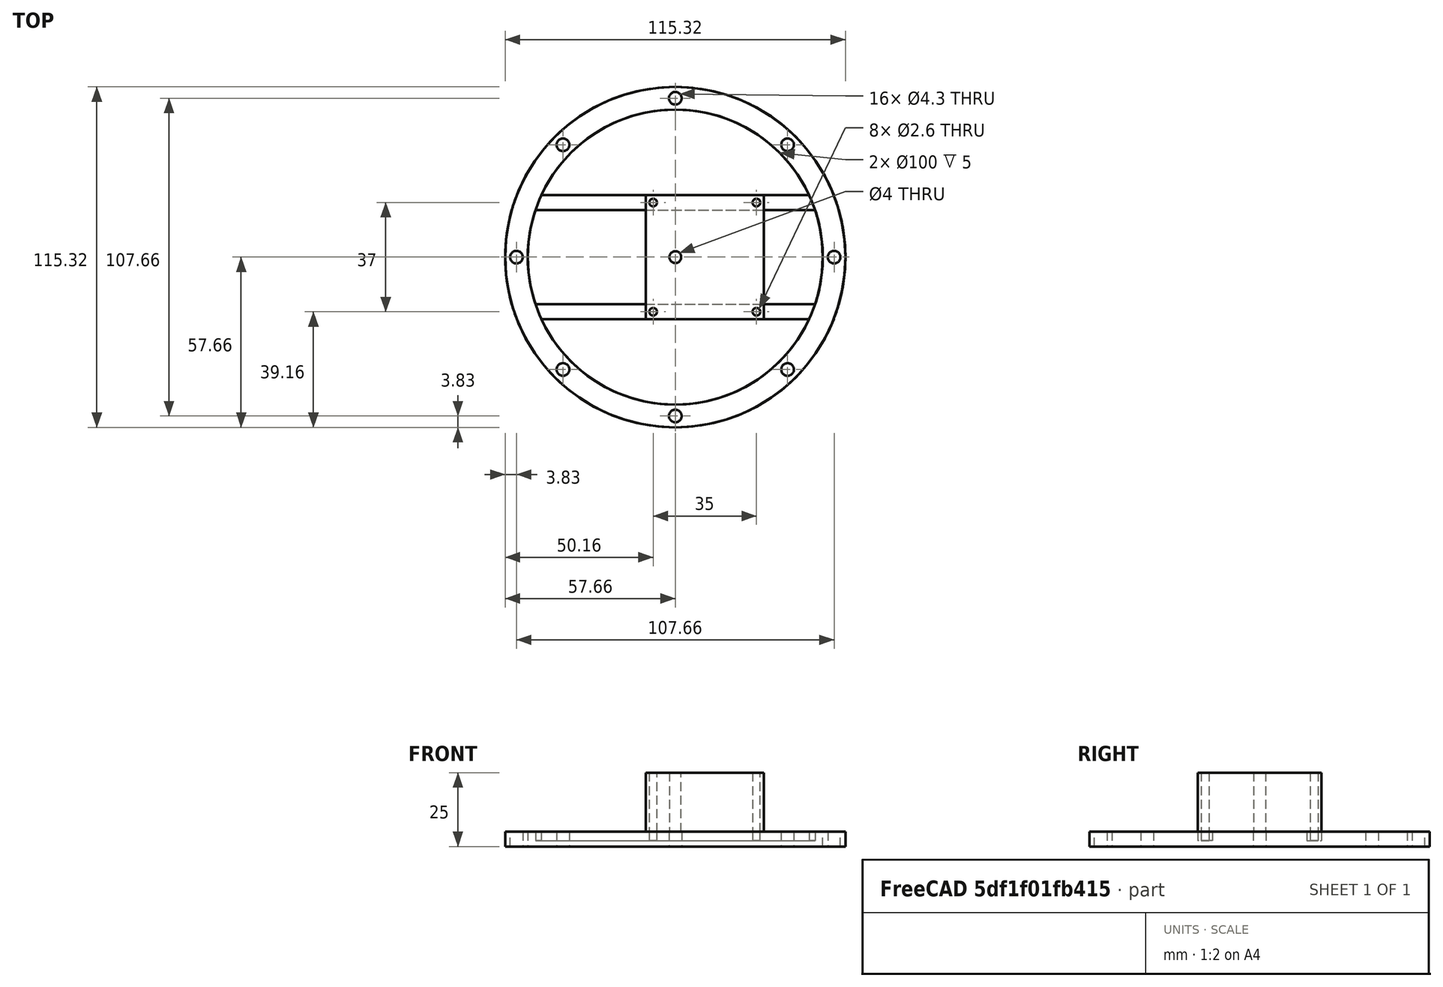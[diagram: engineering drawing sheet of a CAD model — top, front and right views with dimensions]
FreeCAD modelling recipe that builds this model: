
FCSTD DOCUMENT  (FreeCAD 0.20R)
Label: XL30ColumnAttachmentRing_PCBKicker01
License: All rights reserved
LicenseURL: http://en.wikipedia.org/wiki/All_rights_reserved
objects: Part::Cylinder×30, TechDraw::DrawViewDimension×23, Part::Compound×20, Part::Cut×7, TechDraw::DrawProjGroupItem×4, Part::Box×3, Part::MultiFuse×2, TechDraw::DrawSVGTemplate×2, TechDraw::DrawProjGroup×2, TechDraw::DrawPage×2, Part::MultiCommon×1, TechDraw::DrawViewSection×1, TechDraw::DrawViewAnnotation×1
note: 63 computed .brp shape members not serialized (recipe doc carries the construction recipe); baked Part::Feature solids carry a one-line shape summary decoded from their .brp
EXTERNAL_REF file=XL30ColumnAttachmentRing01.FCStd obj=Spreadsheet

FEATURE [Part::Cylinder] Cylinder
  Angle = 360
  AttacherType = Attacher::AttachEngine3D
  FirstAngle = 0
  Height = 5
  Radius = 57.66
  SecondAngle = 0
  expr: Height = <<XL30ColumnAttachmentRing01>>#<<AttachmentRing01>>.ring_thickness
  expr: Radius = <<XL30ColumnAttachmentRing01>>#<<AttachmentRing01>>.ring_od / 2
FEATURE [Part::Cylinder] Cylinder001
  Angle = 360
  AttacherType = Attacher::AttachEngine3D
  FirstAngle = 0
  Height = 5
  Radius = 50
  SecondAngle = 0
  expr: Height = <<XL30ColumnAttachmentRing01>>#<<AttachmentRing01>>.ring_thickness
  expr: Radius = <<XL30ColumnAttachmentRing01>>#<<AttachmentRing01>>.ring_id / 2
FEATURE [Part::Cut] Cut
  Base = -> Cylinder
  Tool = -> Cylinder001
FEATURE [Part::Cylinder] Cylinder002
  Angle = 360
  AttacherType = Attacher::AttachEngine3D
  FirstAngle = 0
  Height = 5
  Placement = pos=(53.83,0,0) rot=(0,0,1;0rad)
  Radius = 2.15
  SecondAngle = 0
  expr: .Placement.Base.x = (<<XL30ColumnAttachmentRing01>>#<<AttachmentRing01>>.ring_od + <<XL30ColumnAttachmentRing01>>#<<AttachmentRing01>>.ring_id) / 4
  expr: Height = <<XL30ColumnAttachmentRing01>>#<<AttachmentRing01>>.ring_thickness
FEATURE [Part::Compound] Compound
  Links = -> [Cylinder002]
FEATURE [Part::Cylinder] Cylinder003
  Angle = 360
  AttacherType = Attacher::AttachEngine3D
  FirstAngle = 0
  Height = 5
  Placement = pos=(53.83,0,0) rot=(0,0,1;0rad)
  Radius = 2.15
  SecondAngle = 0
  expr: .Placement.Base.x = (<<XL30ColumnAttachmentRing01>>#<<AttachmentRing01>>.ring_od + <<XL30ColumnAttachmentRing01>>#<<AttachmentRing01>>.ring_id) / 4
  expr: Height = <<XL30ColumnAttachmentRing01>>#<<AttachmentRing01>>.ring_thickness
FEATURE [Part::Compound] Compound001
  Links = -> [Cylinder003]
  Placement = pos=(0,0,0) rot=(0,0,1;0.785398rad)
FEATURE [Part::Cylinder] Cylinder004
  Angle = 360
  AttacherType = Attacher::AttachEngine3D
  FirstAngle = 0
  Height = 5
  Placement = pos=(53.83,0,0) rot=(0,0,1;0rad)
  Radius = 2.15
  SecondAngle = 0
  expr: .Placement.Base.x = (<<XL30ColumnAttachmentRing01>>#<<AttachmentRing01>>.ring_od + <<XL30ColumnAttachmentRing01>>#<<AttachmentRing01>>.ring_id) / 4
  expr: Height = <<XL30ColumnAttachmentRing01>>#<<AttachmentRing01>>.ring_thickness
FEATURE [Part::Compound] Compound002
  Links = -> [Cylinder004]
  Placement = pos=(0,0,0) rot=(0,0,1;1.5708rad)
FEATURE [Part::Cylinder] Cylinder005
  Angle = 360
  AttacherType = Attacher::AttachEngine3D
  FirstAngle = 0
  Height = 5
  Placement = pos=(53.83,0,0) rot=(0,0,1;0rad)
  Radius = 2.15
  SecondAngle = 0
  expr: .Placement.Base.x = (<<XL30ColumnAttachmentRing01>>#<<AttachmentRing01>>.ring_od + <<XL30ColumnAttachmentRing01>>#<<AttachmentRing01>>.ring_id) / 4
  expr: Height = <<XL30ColumnAttachmentRing01>>#<<AttachmentRing01>>.ring_thickness
FEATURE [Part::Compound] Compound003
  Links = -> [Cylinder005]
  Placement = pos=(0,0,0) rot=(0,0,1;2.35619rad)
FEATURE [Part::Cylinder] Cylinder006
  Angle = 360
  AttacherType = Attacher::AttachEngine3D
  FirstAngle = 0
  Height = 5
  Placement = pos=(53.83,0,0) rot=(0,0,1;0rad)
  Radius = 2.15
  SecondAngle = 0
  expr: .Placement.Base.x = (<<XL30ColumnAttachmentRing01>>#<<AttachmentRing01>>.ring_od + <<XL30ColumnAttachmentRing01>>#<<AttachmentRing01>>.ring_id) / 4
  expr: Height = <<XL30ColumnAttachmentRing01>>#<<AttachmentRing01>>.ring_thickness
FEATURE [Part::Compound] Compound004
  Links = -> [Cylinder006]
  Placement = pos=(0,0,0) rot=(0,0,1;3.14159rad)
FEATURE [Part::Cylinder] Cylinder007
  Angle = 360
  AttacherType = Attacher::AttachEngine3D
  FirstAngle = 0
  Height = 5
  Placement = pos=(53.83,0,0) rot=(0,0,1;0rad)
  Radius = 2.15
  SecondAngle = 0
  expr: .Placement.Base.x = (<<XL30ColumnAttachmentRing01>>#<<AttachmentRing01>>.ring_od + <<XL30ColumnAttachmentRing01>>#<<AttachmentRing01>>.ring_id) / 4
  expr: Height = <<XL30ColumnAttachmentRing01>>#<<AttachmentRing01>>.ring_thickness
FEATURE [Part::Compound] Compound005
  Links = -> [Cylinder007]
  Placement = pos=(0,0,0) rot=(0,0,1;3.92699rad)
FEATURE [Part::Cylinder] Cylinder008
  Angle = 360
  AttacherType = Attacher::AttachEngine3D
  FirstAngle = 0
  Height = 5
  Placement = pos=(53.83,0,0) rot=(0,0,1;0rad)
  Radius = 2.15
  SecondAngle = 0
  expr: .Placement.Base.x = (<<XL30ColumnAttachmentRing01>>#<<AttachmentRing01>>.ring_od + <<XL30ColumnAttachmentRing01>>#<<AttachmentRing01>>.ring_id) / 4
  expr: Height = <<XL30ColumnAttachmentRing01>>#<<AttachmentRing01>>.ring_thickness
FEATURE [Part::Compound] Compound006
  Links = -> [Cylinder008]
  Placement = pos=(0,0,0) rot=(0,0,1;4.71239rad)
FEATURE [Part::Cylinder] Cylinder009
  Angle = 360
  AttacherType = Attacher::AttachEngine3D
  FirstAngle = 0
  Height = 5
  Placement = pos=(53.83,0,0) rot=(0,0,1;0rad)
  Radius = 2.15
  SecondAngle = 0
  expr: .Placement.Base.x = (<<XL30ColumnAttachmentRing01>>#<<AttachmentRing01>>.ring_od + <<XL30ColumnAttachmentRing01>>#<<AttachmentRing01>>.ring_id) / 4
  expr: Height = <<XL30ColumnAttachmentRing01>>#<<AttachmentRing01>>.ring_thickness
FEATURE [Part::Compound] Compound007
  Links = -> [Cylinder009]
  Placement = pos=(0,0,0) rot=(0,0,1;5.49779rad)
FEATURE [Part::Compound] Compound008  label="M4ThroughHoles"
  Links = -> [Compound,Compound001,Compound002,Compound003,Compound004,Compound005,Compound006,Compound007]
FEATURE [Part::Cut] Cut001  label="OuterBaseRing"
  Base = -> Cut
  Tool = -> Compound008
FEATURE [Part::Cylinder] Cylinder010
  Angle = 360
  AttacherType = Attacher::AttachEngine3D
  FirstAngle = 0
  Height = 5
  Radius = 57.66
  SecondAngle = 0
  expr: Height = <<XL30ColumnAttachmentRing01>>#<<AttachmentRing01>>.ring_thickness
  expr: Radius = <<XL30ColumnAttachmentRing01>>#<<AttachmentRing01>>.ring_od / 2
FEATURE [Part::Cylinder] Cylinder011
  Angle = 360
  AttacherType = Attacher::AttachEngine3D
  FirstAngle = 0
  Height = 5
  Radius = 50
  SecondAngle = 0
  expr: Height = <<XL30ColumnAttachmentRing01>>#<<AttachmentRing01>>.ring_thickness
  expr: Radius = <<XL30ColumnAttachmentRing01>>#<<AttachmentRing01>>.ring_id / 2
FEATURE [Part::Cut] Cut002
  Base = -> Cylinder010
  Tool = -> Cylinder011
FEATURE [Part::Cylinder] Cylinder012
  Angle = 360
  AttacherType = Attacher::AttachEngine3D
  FirstAngle = 0
  Height = 5
  Placement = pos=(53.83,0,0) rot=(0,0,1;0rad)
  Radius = 2.15
  SecondAngle = 0
  expr: .Placement.Base.x = (<<XL30ColumnAttachmentRing01>>#<<AttachmentRing01>>.ring_od + <<XL30ColumnAttachmentRing01>>#<<AttachmentRing01>>.ring_id) / 4
  expr: Height = <<XL30ColumnAttachmentRing01>>#<<AttachmentRing01>>.ring_thickness
FEATURE [Part::Compound] Compound009
  Links = -> [Cylinder012]
FEATURE [Part::Cylinder] Cylinder013
  Angle = 360
  AttacherType = Attacher::AttachEngine3D
  FirstAngle = 0
  Height = 5
  Placement = pos=(53.83,0,0) rot=(0,0,1;0rad)
  Radius = 2.15
  SecondAngle = 0
  expr: .Placement.Base.x = (<<XL30ColumnAttachmentRing01>>#<<AttachmentRing01>>.ring_od + <<XL30ColumnAttachmentRing01>>#<<AttachmentRing01>>.ring_id) / 4
  expr: Height = <<XL30ColumnAttachmentRing01>>#<<AttachmentRing01>>.ring_thickness
FEATURE [Part::Compound] Compound010
  Links = -> [Cylinder013]
  Placement = pos=(0,0,0) rot=(0,0,1;0.785398rad)
FEATURE [Part::Cylinder] Cylinder014
  Angle = 360
  AttacherType = Attacher::AttachEngine3D
  FirstAngle = 0
  Height = 5
  Placement = pos=(53.83,0,0) rot=(0,0,1;0rad)
  Radius = 2.15
  SecondAngle = 0
  expr: .Placement.Base.x = (<<XL30ColumnAttachmentRing01>>#<<AttachmentRing01>>.ring_od + <<XL30ColumnAttachmentRing01>>#<<AttachmentRing01>>.ring_id) / 4
  expr: Height = <<XL30ColumnAttachmentRing01>>#<<AttachmentRing01>>.ring_thickness
FEATURE [Part::Compound] Compound011
  Links = -> [Cylinder014]
  Placement = pos=(0,0,0) rot=(0,0,1;1.5708rad)
FEATURE [Part::Cylinder] Cylinder015
  Angle = 360
  AttacherType = Attacher::AttachEngine3D
  FirstAngle = 0
  Height = 5
  Placement = pos=(53.83,0,0) rot=(0,0,1;0rad)
  Radius = 2.15
  SecondAngle = 0
  expr: .Placement.Base.x = (<<XL30ColumnAttachmentRing01>>#<<AttachmentRing01>>.ring_od + <<XL30ColumnAttachmentRing01>>#<<AttachmentRing01>>.ring_id) / 4
  expr: Height = <<XL30ColumnAttachmentRing01>>#<<AttachmentRing01>>.ring_thickness
FEATURE [Part::Compound] Compound012
  Links = -> [Cylinder015]
  Placement = pos=(0,0,0) rot=(0,0,1;2.35619rad)
FEATURE [Part::Cylinder] Cylinder016
  Angle = 360
  AttacherType = Attacher::AttachEngine3D
  FirstAngle = 0
  Height = 5
  Placement = pos=(53.83,0,0) rot=(0,0,1;0rad)
  Radius = 2.15
  SecondAngle = 0
  expr: .Placement.Base.x = (<<XL30ColumnAttachmentRing01>>#<<AttachmentRing01>>.ring_od + <<XL30ColumnAttachmentRing01>>#<<AttachmentRing01>>.ring_id) / 4
  expr: Height = <<XL30ColumnAttachmentRing01>>#<<AttachmentRing01>>.ring_thickness
FEATURE [Part::Compound] Compound013
  Links = -> [Cylinder016]
  Placement = pos=(0,0,0) rot=(0,0,1;3.14159rad)
FEATURE [Part::Cylinder] Cylinder017
  Angle = 360
  AttacherType = Attacher::AttachEngine3D
  FirstAngle = 0
  Height = 5
  Placement = pos=(53.83,0,0) rot=(0,0,1;0rad)
  Radius = 2.15
  SecondAngle = 0
  expr: .Placement.Base.x = (<<XL30ColumnAttachmentRing01>>#<<AttachmentRing01>>.ring_od + <<XL30ColumnAttachmentRing01>>#<<AttachmentRing01>>.ring_id) / 4
  expr: Height = <<XL30ColumnAttachmentRing01>>#<<AttachmentRing01>>.ring_thickness
FEATURE [Part::Compound] Compound014
  Links = -> [Cylinder017]
  Placement = pos=(0,0,0) rot=(0,0,1;3.92699rad)
FEATURE [Part::Cylinder] Cylinder018
  Angle = 360
  AttacherType = Attacher::AttachEngine3D
  FirstAngle = 0
  Height = 5
  Placement = pos=(53.83,0,0) rot=(0,0,1;0rad)
  Radius = 2.15
  SecondAngle = 0
  expr: .Placement.Base.x = (<<XL30ColumnAttachmentRing01>>#<<AttachmentRing01>>.ring_od + <<XL30ColumnAttachmentRing01>>#<<AttachmentRing01>>.ring_id) / 4
  expr: Height = <<XL30ColumnAttachmentRing01>>#<<AttachmentRing01>>.ring_thickness
FEATURE [Part::Compound] Compound015
  Links = -> [Cylinder018]
  Placement = pos=(0,0,0) rot=(0,0,-1;1.5708rad)
FEATURE [Part::Cylinder] Cylinder019
  Angle = 360
  AttacherType = Attacher::AttachEngine3D
  FirstAngle = 0
  Height = 5
  Placement = pos=(53.83,0,0) rot=(0,0,1;0rad)
  Radius = 2.15
  SecondAngle = 0
  expr: .Placement.Base.x = (<<XL30ColumnAttachmentRing01>>#<<AttachmentRing01>>.ring_od + <<XL30ColumnAttachmentRing01>>#<<AttachmentRing01>>.ring_id) / 4
  expr: Height = <<XL30ColumnAttachmentRing01>>#<<AttachmentRing01>>.ring_thickness
FEATURE [Part::Compound] Compound016
  Links = -> [Cylinder019]
  Placement = pos=(0,0,0) rot=(0,0,-1;0.785398rad)
FEATURE [Part::Compound] Compound017  label="M4ThroughHoles001"
  Links = -> [Compound009,Compound010,Compound011,Compound012,Compound013,Compound014,Compound015,Compound016]
FEATURE [Part::Cut] Cut003  label="Ring01"
  Base = -> Cut002
  Tool = -> Compound017
FEATURE [Part::Box] Box  label="Cube"
  AttacherType = Attacher::AttachEngine3D
  Height = 20
  Length = 40
  Width = 42
FEATURE [Part::Cylinder] Cylinder020
  Angle = 360
  AttacherType = Attacher::AttachEngine3D
  FirstAngle = 0
  Height = 20
  Placement = pos=(10,21,0) rot=(0,0,1;0rad)
  Radius = 2
  SecondAngle = 0
FEATURE [Part::Cut] Cut004
  Base = -> Box
  Tool = -> Cylinder020
FEATURE [Part::Cylinder] Cylinder021
  Angle = 360
  AttacherType = Attacher::AttachEngine3D
  FirstAngle = 0
  Height = 20
  Placement = pos=(2.5,2.5,0) rot=(0,0,1;0rad)
  Radius = 1.3
  SecondAngle = 0
FEATURE [Part::Cylinder] Cylinder022
  Angle = 360
  AttacherType = Attacher::AttachEngine3D
  FirstAngle = 0
  Height = 20
  Placement = pos=(37.5,2.5,0) rot=(0,0,1;0rad)
  Radius = 1.3
  SecondAngle = 0
FEATURE [Part::Cylinder] Cylinder023
  Angle = 360
  AttacherType = Attacher::AttachEngine3D
  FirstAngle = 0
  Height = 20
  Placement = pos=(2.5,39.5,0) rot=(0,0,1;0rad)
  Radius = 1.3
  SecondAngle = 0
FEATURE [Part::Cylinder] Cylinder024
  Angle = 360
  AttacherType = Attacher::AttachEngine3D
  FirstAngle = 0
  Height = 20
  Placement = pos=(37.5,39.5,0) rot=(0,0,1;0rad)
  Radius = 1.3
  SecondAngle = 0
FEATURE [Part::Compound] Compound018
  Links = -> [Cylinder021,Cylinder022,Cylinder023,Cylinder024]
FEATURE [Part::Cut] Cut005  label="PCBStackTemplate"
  Base = -> Cut004
  Placement = pos=(-10,-21,5) rot=(0,0,1;0rad)
  Tool = -> Compound018
FEATURE [Part::Cylinder] Cylinder025
  Angle = 360
  AttacherType = Attacher::AttachEngine3D
  FirstAngle = 0
  Height = 20
  Placement = pos=(2.5,2.5,0) rot=(0,0,1;0rad)
  Radius = 1.3
  SecondAngle = 0
FEATURE [Part::Cylinder] Cylinder026
  Angle = 360
  AttacherType = Attacher::AttachEngine3D
  FirstAngle = 0
  Height = 20
  Placement = pos=(37.5,2.5,0) rot=(0,0,1;0rad)
  Radius = 1.3
  SecondAngle = 0
FEATURE [Part::Cylinder] Cylinder027
  Angle = 360
  AttacherType = Attacher::AttachEngine3D
  FirstAngle = 0
  Height = 20
  Placement = pos=(2.5,39.5,0) rot=(0,0,1;0rad)
  Radius = 1.3
  SecondAngle = 0
FEATURE [Part::Cylinder] Cylinder028
  Angle = 360
  AttacherType = Attacher::AttachEngine3D
  FirstAngle = 0
  Height = 20
  Placement = pos=(37.5,39.5,0) rot=(0,0,1;0rad)
  Radius = 1.3
  SecondAngle = 0
FEATURE [Part::Compound] Compound019  label="M3Mountholes"
  Links = -> [Cylinder025,Cylinder026,Cylinder027,Cylinder028]
  Placement = pos=(-10,-21,0) rot=(0,0,1;0rad)
FEATURE [Part::Box] Box001  label="Cube001"
  AttacherType = Attacher::AttachEngine3D
  Height = 3
  Length = 115.32
  Placement = pos=(-57.66,-21,2) rot=(0,0,1;0rad)
  Width = 5
  expr: .Placement.Base.x = -<<XL30ColumnAttachmentRing01>>#<<AttachmentRing01>>.ring_od / 2
  expr: .Placement.Base.z = <<XL30ColumnAttachmentRing01>>#<<AttachmentRing01>>.ring_thickness - 3
  expr: Length = <<XL30ColumnAttachmentRing01>>#<<AttachmentRing01>>.ring_od
FEATURE [Part::Box] Box002  label="Cube002"
  AttacherType = Attacher::AttachEngine3D
  Height = 3
  Length = 115.32
  Placement = pos=(-57.66,16,2) rot=(0,0,1;0rad)
  Width = 5
  expr: .Placement.Base.x = -<<XL30ColumnAttachmentRing01>>#<<AttachmentRing01>>.ring_od / 2
  expr: .Placement.Base.z = <<XL30ColumnAttachmentRing01>>#<<AttachmentRing01>>.ring_thickness - 3
  expr: Length = <<XL30ColumnAttachmentRing01>>#<<AttachmentRing01>>.ring_od
FEATURE [Part::MultiFuse] Fusion
  Shapes = -> [Box001,Box002]
FEATURE [Part::Cylinder] Cylinder029
  Angle = 360
  AttacherType = Attacher::AttachEngine3D
  FirstAngle = 0
  Height = 5
  Radius = 57.66
  SecondAngle = 0
  expr: Height = <<XL30ColumnAttachmentRing01>>#<<AttachmentRing01>>.ring_thickness
  expr: Radius = <<XL30ColumnAttachmentRing01>>#<<AttachmentRing01>>.ring_od / 2
FEATURE [Part::MultiCommon] Common
  Shapes = -> [Fusion,Cylinder029]
FEATURE [Part::Cut] Cut006
  Base = -> Common
  Tool = -> Compound019
FEATURE [Part::MultiFuse] Fusion001  label="Stackmountring01"
  Shapes = -> [Cut003,Cut006]
FEATURE [TechDraw::DrawSVGTemplate] Template
  EditableTexts = Designed_by_Name=Thomas Spielauer; FC-Date=2023-11-15; FC-SC=mm; FC-SH=1/1; FC-Title=XL30 column cage: PCB mount; Subtitle=Compatible with XL30 column attachment ring
  Height = 210
  Orientation = 1
  Width = 297
FEATURE [TechDraw::DrawProjGroupItem] ProjItem  label="Front"
  CoarseView = false
  Direction = (0,0,1)
  Focus = 100
  HardHidden = false
  IsoCount = 0
  IsoHidden = false
  IsoVisible = false
  LockPosition = true
  Perspective = false
  Rotation = 0
  RotationVector = (1,0,0)
  ScaleType = 2
  SeamHidden = false
  SeamVisible = true
  SmoothHidden = false
  SmoothVisible = true
  Source = -> [Fusion001]
  Type = 0
  X = 0
  XDirection = (1,0,0)
  Y = 0
FEATURE [TechDraw::DrawProjGroupItem] ProjItem002  label="Top"
  CoarseView = false
  Direction = (0,1,0)
  Focus = 100
  HardHidden = false
  IsoCount = 0
  IsoHidden = false
  IsoVisible = false
  LockPosition = false
  Perspective = false
  Rotation = 0
  RotationVector = (1,0,0)
  ScaleType = 2
  SeamHidden = false
  SeamVisible = true
  SmoothHidden = false
  SmoothVisible = true
  Source = -> [Fusion001]
  Type = 4
  X = 0
  XDirection = (1,0,0)
  Y = -130.32
FEATURE [TechDraw::DrawProjGroup] ProjGroup
  Anchor = -> ProjItem
  AutoDistribute = true
  LockPosition = false
  ProjectionType = 0
  Rotation = 0
  ScaleType = 0
  Source = -> [Fusion001]
  Views = -> [ProjItem,ProjItem002]
  X = 77.9531
  Y = 128.789
  spacingX = 15
  spacingY = 15
FEATURE [TechDraw::DrawViewSection] SectionView  label="Section  - "
  BaseView = -> ProjItem
  CoarseView = false
  CutSurfaceDisplay = 2
  Direction = (-1,0,0)
  FileGeomPattern = <path>
  FileHatchPattern = <path>
  Focus = 100
  FuseBeforeCut = false
  HardHidden = false
  HatchScale = 1
  IsoCount = 0
  IsoHidden = false
  IsoVisible = false
  LockPosition = false
  NameGeomPattern = Diamond
  Perspective = false
  Rotation = 0
  ScaleType = 2
  SeamHidden = false
  SeamVisible = true
  SectionDirection = 0
  SectionNormal = (-1,0,0)
  SectionOrigin = (0,0,2.5)
  SmoothHidden = false
  SmoothVisible = true
  Source = -> [Fusion001]
  X = 175.93
  XDirection = (0,0,1)
  Y = 127.772
FEATURE [TechDraw::DrawViewDimension] Dimension
  AngleOverride = false
  Arbitrary = false
  ArbitraryTolerances = false
  EqualTolerance = true
  ExtensionAngle = 0
  FormatSpec = ⌀%.2w
  FormatSpecOverTolerance = %+.2w
  FormatSpecUnderTolerance = %+.2w
  Inverted = false
  LineAngle = 0
  LockPosition = false
  MeasureType = 1
  OverTolerance = 0
  References2D = -> [ProjItem]
  Rotation = 0
  ScaleType = 0
  TheoreticalExact = false
  Type = 5
  UnderTolerance = 0
  X = 61.5234
  Y = 45.459
FEATURE [TechDraw::DrawViewDimension] Dimension001
  AngleOverride = false
  Arbitrary = false
  ArbitraryTolerances = false
  EqualTolerance = true
  ExtensionAngle = 0
  FormatSpec = ⌀%.2w
  FormatSpecOverTolerance = %+.2w
  FormatSpecUnderTolerance = %+.2w
  Inverted = false
  LineAngle = 0
  LockPosition = false
  MeasureType = 1
  OverTolerance = 0
  References2D = -> [ProjItem]
  Rotation = 0
  ScaleType = 0
  TheoreticalExact = false
  Type = 5
  UnderTolerance = 0
  X = 66.6504
  Y = 36.5723
FEATURE [TechDraw::DrawViewDimension] Dimension002
  AngleOverride = false
  Arbitrary = false
  ArbitraryTolerances = false
  EqualTolerance = true
  ExtensionAngle = 0
  FormatSpec = ⌀%.2w (8x)
  FormatSpecOverTolerance = %+.2w
  FormatSpecUnderTolerance = %+.2w
  Inverted = false
  LineAngle = 0
  LockPosition = false
  MeasureType = 1
  OverTolerance = 0
  References2D = -> [ProjItem]
  Rotation = 0
  ScaleType = 0
  TheoreticalExact = false
  Type = 5
  UnderTolerance = 0
  X = 54.0039
  Y = 54.0039
FEATURE [TechDraw::DrawViewDimension] Dimension003
  AngleOverride = false
  Arbitrary = false
  ArbitraryTolerances = false
  EqualTolerance = true
  ExtensionAngle = 0
  FormatSpec = ⌀%.2w (4x M3)
  FormatSpecOverTolerance = %+.2w
  FormatSpecUnderTolerance = %+.2w
  Inverted = false
  LineAngle = 0
  LockPosition = false
  MeasureType = 1
  OverTolerance = 0
  References2D = -> [ProjItem]
  Rotation = 0
  ScaleType = 0
  TheoreticalExact = false
  Type = 5
  UnderTolerance = 0
  X = -25.2791
  Y = 6.47025
FEATURE [TechDraw::DrawViewDimension] Dimension004
  AngleOverride = false
  Arbitrary = false
  ArbitraryTolerances = false
  EqualTolerance = true
  ExtensionAngle = 0
  FormatSpec = ⌀%.2w
  FormatSpecOverTolerance = %+.2w
  FormatSpecUnderTolerance = %+.2w
  Inverted = false
  LineAngle = 0
  LockPosition = false
  MeasureType = 1
  OverTolerance = 0
  References2D = -> [ProjItem]
  Rotation = 0
  ScaleType = 0
  TheoreticalExact = false
  Type = 5
  UnderTolerance = 0
  X = 70.0684
  Y = 28.1982
FEATURE [TechDraw::DrawViewDimension] Dimension005
  AngleOverride = false
  Arbitrary = false
  ArbitraryTolerances = false
  EqualTolerance = true
  ExtensionAngle = 0
  FormatSpec = %.2w
  FormatSpecOverTolerance = %+.2w
  FormatSpecUnderTolerance = %+.2w
  Inverted = false
  LineAngle = 0
  LockPosition = false
  MeasureType = 1
  OverTolerance = 0
  References2D = -> [ProjItem]
  Rotation = 0
  ScaleType = 0
  TheoreticalExact = false
  Type = 6
  UnderTolerance = 0
  X = -32.2741
  Y = 59.9027
FEATURE [TechDraw::DrawViewDimension] Dimension006
  AngleOverride = false
  Arbitrary = false
  ArbitraryTolerances = false
  EqualTolerance = true
  ExtensionAngle = 0
  FormatSpec = %.2w
  FormatSpecOverTolerance = %+.2w
  FormatSpecUnderTolerance = %+.2w
  Inverted = false
  LineAngle = 0
  LockPosition = false
  MeasureType = 1
  OverTolerance = 0
  References2D = -> [ProjItem]
  Rotation = 0
  ScaleType = 0
  TheoreticalExact = false
  Type = 2
  UnderTolerance = 0
  X = 31.0643
  Y = -6.39286
FEATURE [TechDraw::DrawViewDimension] Dimension007
  AngleOverride = false
  Arbitrary = false
  ArbitraryTolerances = false
  EqualTolerance = true
  ExtensionAngle = 0
  FormatSpec = %.2w
  FormatSpecOverTolerance = %+.2w
  FormatSpecUnderTolerance = %+.2w
  Inverted = false
  LineAngle = 0
  LockPosition = false
  MeasureType = 1
  OverTolerance = 0
  References2D = -> [ProjItem]
  Rotation = 0
  ScaleType = 0
  TheoreticalExact = false
  Type = 2
  UnderTolerance = 0
  X = 31.3208
  Y = 10.3055
FEATURE [TechDraw::DrawViewDimension] Dimension008
  AngleOverride = false
  Arbitrary = false
  ArbitraryTolerances = false
  EqualTolerance = true
  ExtensionAngle = 0
  FormatSpec = %.2w
  FormatSpecOverTolerance = %+.2w
  FormatSpecUnderTolerance = %+.2w
  Inverted = false
  LineAngle = 0
  LockPosition = false
  MeasureType = 1
  OverTolerance = 0
  References2D = -> [ProjItem]
  Rotation = 0
  ScaleType = 0
  TheoreticalExact = false
  Type = 1
  UnderTolerance = 0
  X = -4.11113
  Y = 33.5088
FEATURE [TechDraw::DrawViewDimension] Dimension009
  AngleOverride = false
  Arbitrary = false
  ArbitraryTolerances = false
  EqualTolerance = true
  ExtensionAngle = 0
  FormatSpec = %.2w
  FormatSpecOverTolerance = %+.2w
  FormatSpecUnderTolerance = %+.2w
  Inverted = false
  LineAngle = 0
  LockPosition = false
  MeasureType = 1
  OverTolerance = 0
  References2D = -> [ProjItem]
  Rotation = 0
  ScaleType = 0
  TheoreticalExact = false
  Type = 1
  UnderTolerance = 0
  X = 14.1111
  Y = 36.2173
FEATURE [TechDraw::DrawViewDimension] Dimension010
  AngleOverride = false
  Arbitrary = false
  ArbitraryTolerances = false
  EqualTolerance = true
  ExtensionAngle = 0
  FormatSpec = %.2w
  FormatSpecOverTolerance = %+.2w
  FormatSpecUnderTolerance = %+.2w
  Inverted = false
  LineAngle = 0
  LockPosition = false
  MeasureType = 1
  OverTolerance = 0
  References2D = -> [ProjItem]
  Rotation = 0
  ScaleType = 0
  TheoreticalExact = false
  Type = 2
  UnderTolerance = 0
  X = -65.7891
  Y = 30.0196
FEATURE [TechDraw::DrawViewDimension] Dimension011
  AngleOverride = false
  Arbitrary = false
  ArbitraryTolerances = false
  EqualTolerance = true
  ExtensionAngle = 0
  FormatSpec = %.2w
  FormatSpecOverTolerance = %+.2w
  FormatSpecUnderTolerance = %+.2w
  Inverted = false
  LineAngle = 0
  LockPosition = false
  MeasureType = 1
  OverTolerance = 0
  References2D = -> [SectionView]
  Rotation = 0
  ScaleType = 0
  TheoreticalExact = false
  Type = 1
  UnderTolerance = 0
  X = 7.50034
  Y = -8.08305
FEATURE [TechDraw::DrawViewDimension] Dimension012
  AngleOverride = false
  Arbitrary = false
  ArbitraryTolerances = false
  EqualTolerance = true
  ExtensionAngle = 0
  FormatSpec = %.2w
  FormatSpecOverTolerance = %+.2w
  FormatSpecUnderTolerance = %+.2w
  Inverted = false
  LineAngle = 0
  LockPosition = false
  MeasureType = 1
  OverTolerance = 0
  References2D = -> [SectionView]
  Rotation = 0
  ScaleType = 0
  TheoreticalExact = false
  Type = 1
  UnderTolerance = 0
  X = 15.8175
  Y = -53.6967
FEATURE [TechDraw::DrawViewDimension] Dimension013
  AngleOverride = false
  Arbitrary = false
  ArbitraryTolerances = false
  EqualTolerance = true
  ExtensionAngle = 0
  FormatSpec = %.2w
  FormatSpecOverTolerance = %+.2w
  FormatSpecUnderTolerance = %+.2w
  Inverted = false
  LineAngle = 0
  LockPosition = false
  MeasureType = 1
  OverTolerance = 0
  References2D = -> [SectionView]
  Rotation = 0
  ScaleType = 0
  TheoreticalExact = false
  Type = 2
  UnderTolerance = 0
  X = 13.592
  Y = 47.9705
FEATURE [TechDraw::DrawViewDimension] Dimension014
  AngleOverride = false
  Arbitrary = false
  ArbitraryTolerances = false
  EqualTolerance = true
  ExtensionAngle = 0
  FormatSpec = %.2w
  FormatSpecOverTolerance = %+.2w
  FormatSpecUnderTolerance = %+.2w
  Inverted = false
  LineAngle = 0
  LockPosition = false
  MeasureType = 1
  OverTolerance = 0
  References2D = -> [ProjItem002]
  Rotation = 0
  ScaleType = 0
  TheoreticalExact = false
  Type = 1
  UnderTolerance = 0
  X = -0.474718
  Y = 10.9185
FEATURE [TechDraw::DrawViewDimension] Dimension015
  AngleOverride = false
  Arbitrary = false
  ArbitraryTolerances = false
  EqualTolerance = true
  ExtensionAngle = 0
  FormatSpec = %.2w
  FormatSpecOverTolerance = %+.2w
  FormatSpecUnderTolerance = %+.2w
  Inverted = false
  LineAngle = 0
  LockPosition = false
  MeasureType = 1
  OverTolerance = 0
  References2D = -> [ProjItem002]
  Rotation = 0
  ScaleType = 0
  TheoreticalExact = false
  Type = 2
  UnderTolerance = 0
  X = -65.4543
  Y = 12.2317
FEATURE [TechDraw::DrawViewAnnotation] Annotation
  Font = osifont
  LineSpace = 80
  LockPosition = false
  MaxWidth = -1
  Rotation = 0
  ScaleType = 0
  Text = Ring with 8x 4.3mm through holes | (for M4 threaded rods passing | through). Ring is 5mm thick, | two beams crossing, beams are | 3mm thick and have 4x M3 threads
  TextSize = 5
  TextStyle = 0
  X = 241.195
  Y = 166.934
FEATURE [TechDraw::DrawPage] Page
  KeepUpdated = true
  NextBalloonIndex = 1
  ProjectionType = 0
  Template = -> Template
  Views = -> [ProjGroup,SectionView,Dimension,Dimension001,Dimension002,Dimension003,Dimension004,Dimension005,Dimension006,Dimension007,Dimension008,Dimension009,Dimension010,Dimension011,Dimension012,Dimension013,Dimension014,Dimension015,Annotation]
FEATURE [TechDraw::DrawSVGTemplate] Template001
  EditableTexts = Designed_by_Name=Thomas Spielauer; FC-Date=2023-11-15; FC-SC=mm; FC-SH=1/1; FC-Title=XL30 Attachment Base Ring; Subtitle=Base ring for stability
  Height = 210
  Orientation = 1
  Width = 297
FEATURE [TechDraw::DrawProjGroupItem] ProjItem003  label="Front001"
  CoarseView = false
  Direction = (0,0,1)
  Focus = 100
  HardHidden = false
  IsoCount = 0
  IsoHidden = false
  IsoVisible = false
  LockPosition = true
  Perspective = false
  Rotation = 0
  RotationVector = (1,0,0)
  ScaleType = 2
  SeamHidden = false
  SeamVisible = true
  SmoothHidden = false
  SmoothVisible = true
  Source = -> [Cut001]
  Type = 0
  X = 0
  XDirection = (1,0,0)
  Y = 0
FEATURE [TechDraw::DrawProjGroupItem] ProjItem004  label="Left"
  CoarseView = false
  Direction = (-1,0,1e-16)
  Focus = 100
  HardHidden = false
  IsoCount = 0
  IsoHidden = false
  IsoVisible = false
  LockPosition = false
  Perspective = false
  Rotation = 0
  RotationVector = (1,0,0)
  ScaleType = 2
  SeamHidden = false
  SeamVisible = true
  SmoothHidden = false
  SmoothVisible = true
  Source = -> [Cut001]
  Type = 1
  X = 87.2041
  XDirection = (1e-16,0,1)
  Y = 0
FEATURE [TechDraw::DrawProjGroup] ProjGroup001
  Anchor = -> ProjItem003
  AutoDistribute = true
  LockPosition = false
  ProjectionType = 0
  Rotation = 0
  ScaleType = 0
  Source = -> [Cut001]
  Views = -> [ProjItem003,ProjItem004]
  X = 98.0508
  Y = 130.02
  spacingX = 15
  spacingY = 15
FEATURE [TechDraw::DrawViewDimension] Dimension016
  AngleOverride = false
  Arbitrary = false
  ArbitraryTolerances = false
  EqualTolerance = true
  ExtensionAngle = 0
  FormatSpec = ⌀%.2w
  FormatSpecOverTolerance = %+.2w
  FormatSpecUnderTolerance = %+.2w
  Inverted = false
  LineAngle = 0
  LockPosition = false
  MeasureType = 1
  OverTolerance = 0
  References2D = -> [ProjItem003]
  Rotation = 0
  ScaleType = 0
  TheoreticalExact = false
  Type = 5
  UnderTolerance = 0
  X = 30.1616
  Y = 3.90021
FEATURE [TechDraw::DrawViewDimension] Dimension017
  AngleOverride = false
  Arbitrary = false
  ArbitraryTolerances = false
  EqualTolerance = true
  ExtensionAngle = 0
  FormatSpec = ⌀%.2w
  FormatSpecOverTolerance = %+.2w
  FormatSpecUnderTolerance = %+.2w
  Inverted = false
  LineAngle = 0
  LockPosition = false
  MeasureType = 1
  OverTolerance = 0
  References2D = -> [ProjItem003]
  Rotation = 0
  ScaleType = 0
  TheoreticalExact = false
  Type = 5
  UnderTolerance = 0
  X = 25.7414
  Y = 11.9606
FEATURE [TechDraw::DrawViewDimension] Dimension018
  AngleOverride = false
  Arbitrary = false
  ArbitraryTolerances = false
  EqualTolerance = true
  ExtensionAngle = 0
  FormatSpec = ⌀%.2w
  FormatSpecOverTolerance = %+.2w
  FormatSpecUnderTolerance = %+.2w
  Inverted = false
  LineAngle = 0
  LockPosition = false
  MeasureType = 1
  OverTolerance = 0
  References2D = -> [ProjItem003]
  Rotation = 0
  ScaleType = 0
  TheoreticalExact = false
  Type = 5
  UnderTolerance = 0
  X = -12.5673
  Y = 35.3185
FEATURE [TechDraw::DrawViewDimension] Dimension019
  AngleOverride = false
  Arbitrary = false
  ArbitraryTolerances = false
  EqualTolerance = true
  ExtensionAngle = 0
  FormatSpec = ⌀%.2w (8x)
  FormatSpecOverTolerance = %+.2w
  FormatSpecUnderTolerance = %+.2w
  Inverted = false
  LineAngle = 0
  LockPosition = false
  MeasureType = 1
  OverTolerance = 0
  References2D = -> [ProjItem003]
  Rotation = 0
  ScaleType = 0
  TheoreticalExact = false
  Type = 5
  UnderTolerance = 0
  X = 56.1196
  Y = 45.9358
FEATURE [TechDraw::DrawViewDimension] Dimension020
  AngleOverride = false
  Arbitrary = false
  ArbitraryTolerances = false
  EqualTolerance = true
  ExtensionAngle = 0
  FormatSpec = %.2w
  FormatSpecOverTolerance = %+.2w
  FormatSpecUnderTolerance = %+.2w
  Inverted = false
  LineAngle = 0
  LockPosition = false
  MeasureType = 1
  OverTolerance = 0
  References2D = -> [ProjItem004]
  Rotation = 0
  ScaleType = 0
  TheoreticalExact = false
  Type = 1
  UnderTolerance = 0
  X = 16.1
  Y = 67.274
FEATURE [TechDraw::DrawViewDimension] Dimension021
  AngleOverride = false
  Arbitrary = false
  ArbitraryTolerances = false
  EqualTolerance = true
  ExtensionAngle = 0
  FormatSpec = %.2w
  FormatSpecOverTolerance = %+.2w
  FormatSpecUnderTolerance = %+.2w
  Inverted = false
  LineAngle = 0
  LockPosition = false
  MeasureType = 1
  OverTolerance = 0
  References2D = -> [ProjItem004]
  Rotation = 0
  ScaleType = 0
  TheoreticalExact = false
  Type = 2
  UnderTolerance = 0
  X = -13.2256
  Y = 1.37674
FEATURE [TechDraw::DrawViewDimension] Dimension022
  AngleOverride = false
  Arbitrary = false
  ArbitraryTolerances = false
  EqualTolerance = true
  ExtensionAngle = 0
  FormatSpec = %.2w
  FormatSpecOverTolerance = %+.2w
  FormatSpecUnderTolerance = %+.2w
  Inverted = false
  LineAngle = 0
  LockPosition = false
  MeasureType = 1
  OverTolerance = 0
  References2D = -> [ProjItem003]
  Rotation = 0
  ScaleType = 0
  TheoreticalExact = false
  Type = 6
  UnderTolerance = 0
  X = -55.542
  Y = 41.3005
FEATURE [TechDraw::DrawPage] Page001
  KeepUpdated = true
  NextBalloonIndex = 1
  ProjectionType = 0
  Template = -> Template001
  Views = -> [ProjGroup001,Dimension016,Dimension017,Dimension018,Dimension019,Dimension020,Dimension021,Dimension022]
note: 2 file-system paths scrubbed to <path> (originals preserved in the JSON sidecar)
